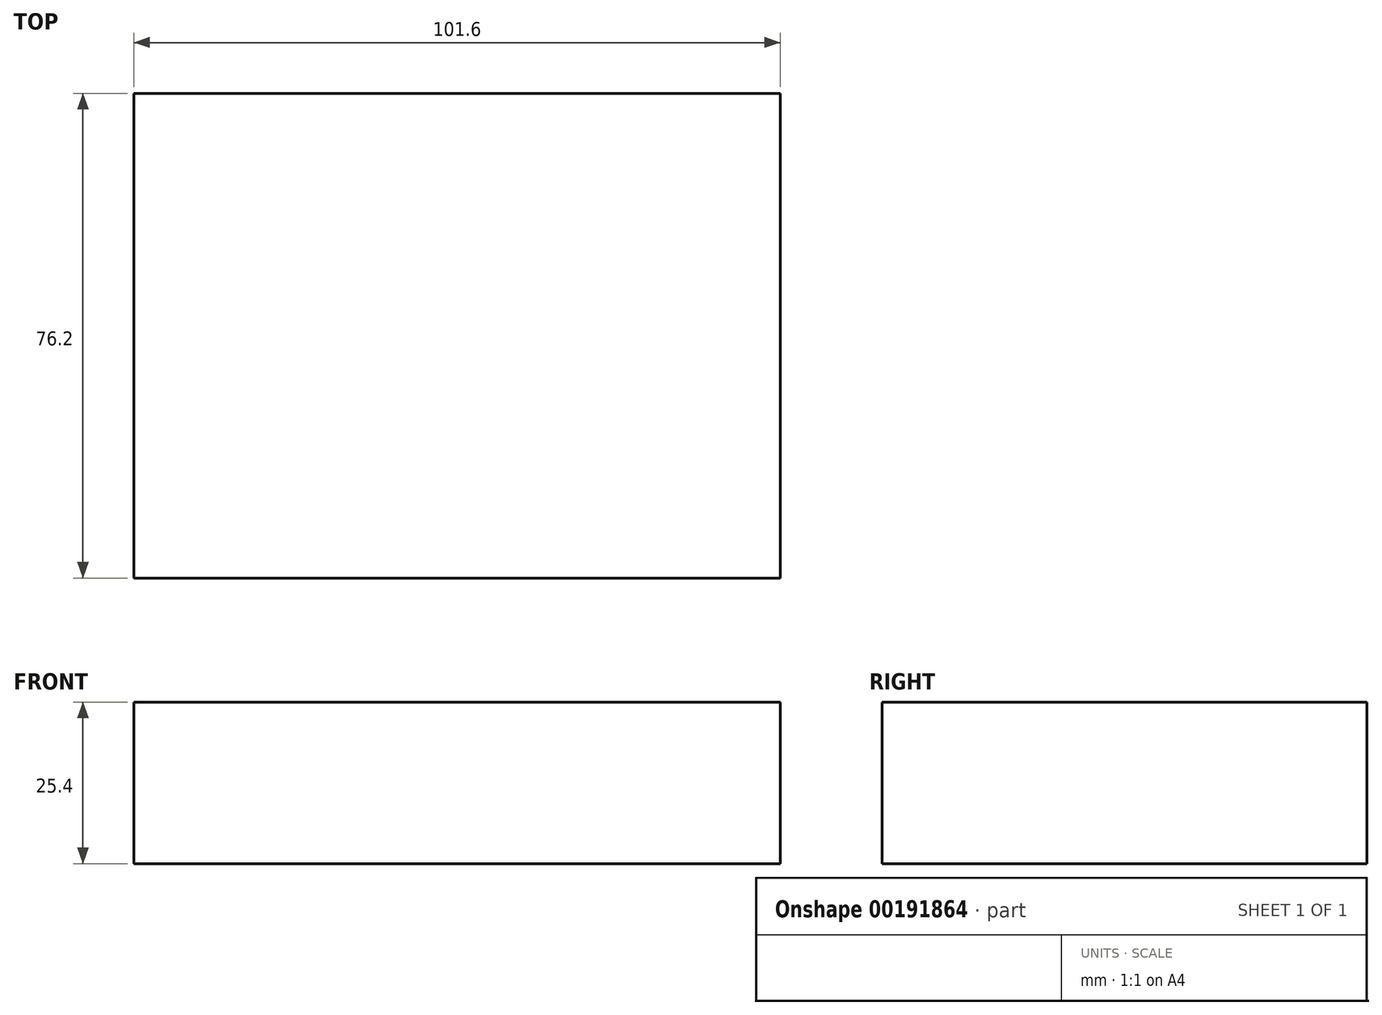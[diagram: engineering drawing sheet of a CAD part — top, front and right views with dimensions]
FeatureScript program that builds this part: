
annotation { "Feature Type Name" : "Feature", "Feature Type Description" : "" }
export const myFeature = defineFeature(function(context is Context, id is Id, definition is map)
    precondition{}
    {
        {
            var Q0;
            Q0=qCreatedBy(makeId("Top.planeOp"),FACE);
            var sketch = newSketch(context, id + "F0", { "sketchPlane" : qUnion([Q0])});
            skLineSegment(sketch, "E0.bottom", {"start": v(-48.9, -43.34) * mm, "end": v(52.7, -43.34) * mm});
            skLineSegment(sketch, "E0.top", {"start": v(-48.9, 32.86) * mm, "end": v(52.7, 32.86) * mm});
            skLineSegment(sketch, "E0.left", {"start": v(-48.9, -43.34) * mm, "end": v(-48.9, 32.86) * mm});
            skLineSegment(sketch, "E0.right", {"start": v(52.7, -43.34) * mm, "end": v(52.7, 32.86) * mm});
            skSolve(sketch);
        }
        {
            var Q0;
            Q0=makeQuery(id+"F0.imprint","IMPRINT",FACE,{"disambiguationData":[TD([[makeQuery(id+"F0.imprint","IMPRINT",EDGE,{"derivedFrom":sQuery(id+"F0.wireOp",EDGE,"E0.bottom")}),1.0]])]});
            extrude(context, id + "F1", {"entities" : qUnion([Q0]), "depth" : 25.4 * mm});
        }
    });
